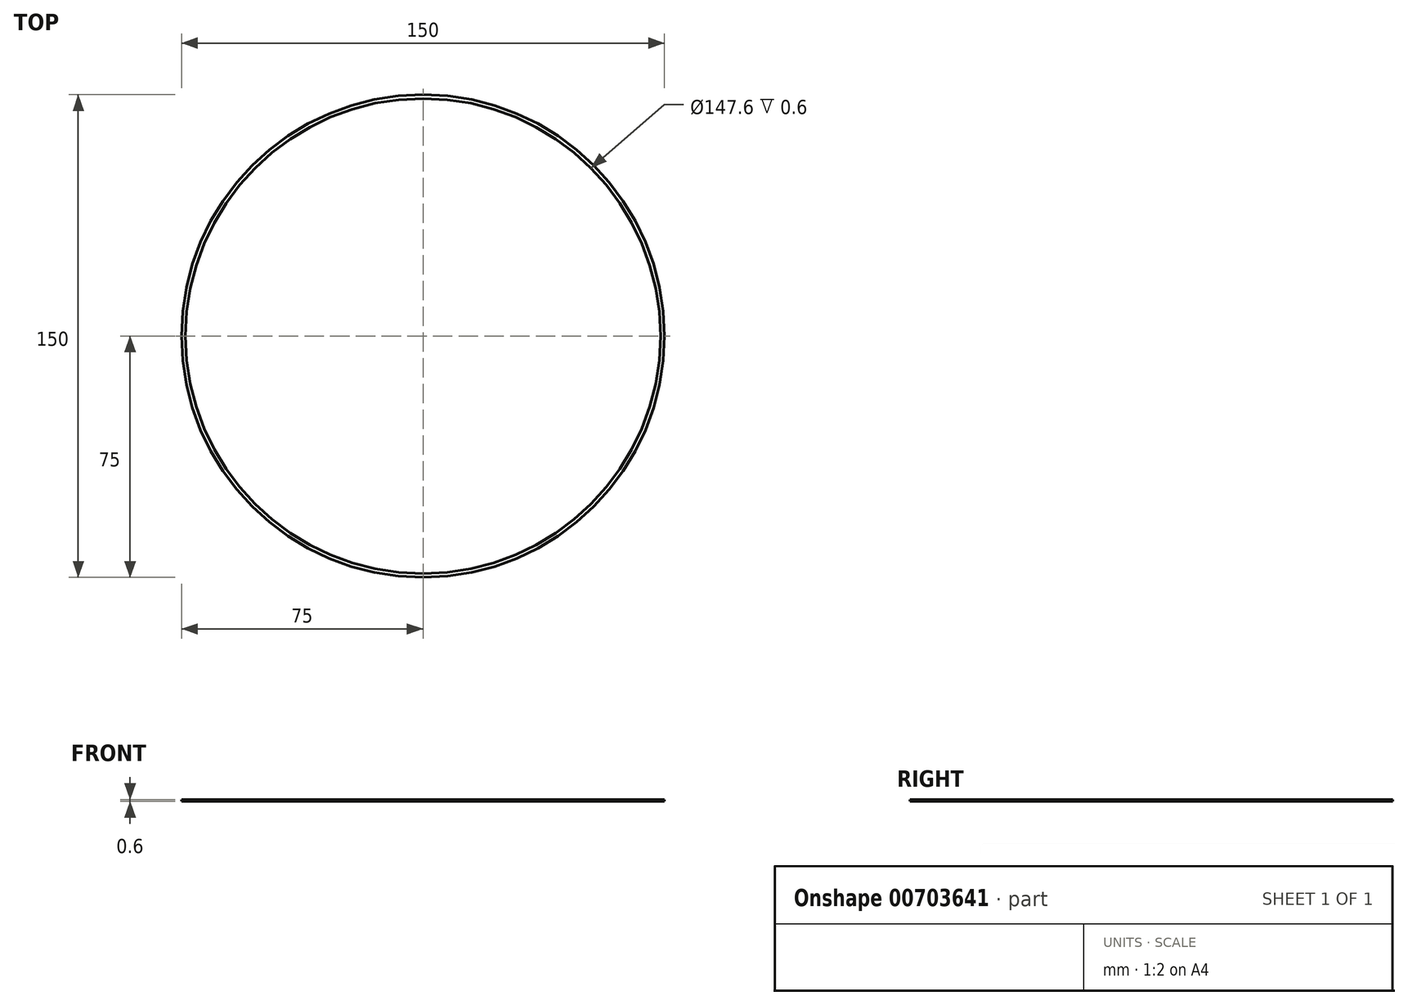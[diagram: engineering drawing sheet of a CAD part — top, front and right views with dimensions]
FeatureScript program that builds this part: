
annotation { "Feature Type Name" : "Feature", "Feature Type Description" : "" }
export const myFeature = defineFeature(function(context is Context, id is Id, definition is map)
    precondition{}
    {
        {
            var Q0;
            Q0=qCreatedBy(makeId("Top.planeOp"),FACE);
            var sketch = newSketch(context, id + "F0", { "sketchPlane" : qUnion([Q0])});
            skCircle(sketch, "E0", {"center": v(0, 0) * mm, "radius": 75 * mm});
            skCircle(sketch, "E1.0", {"center": v(0, 0) * mm, "radius": 73.8 * mm});
            skSolve(sketch);
        }
        {
            var Q0;
            Q0=qSketchRegion(id+"F0",true);
            extrude(context, id + "F1", {"entities" : qUnion([Q0]), "depth" : .6 * mm, "offsetDistance" : 25.4 * mm});
        }
    });
